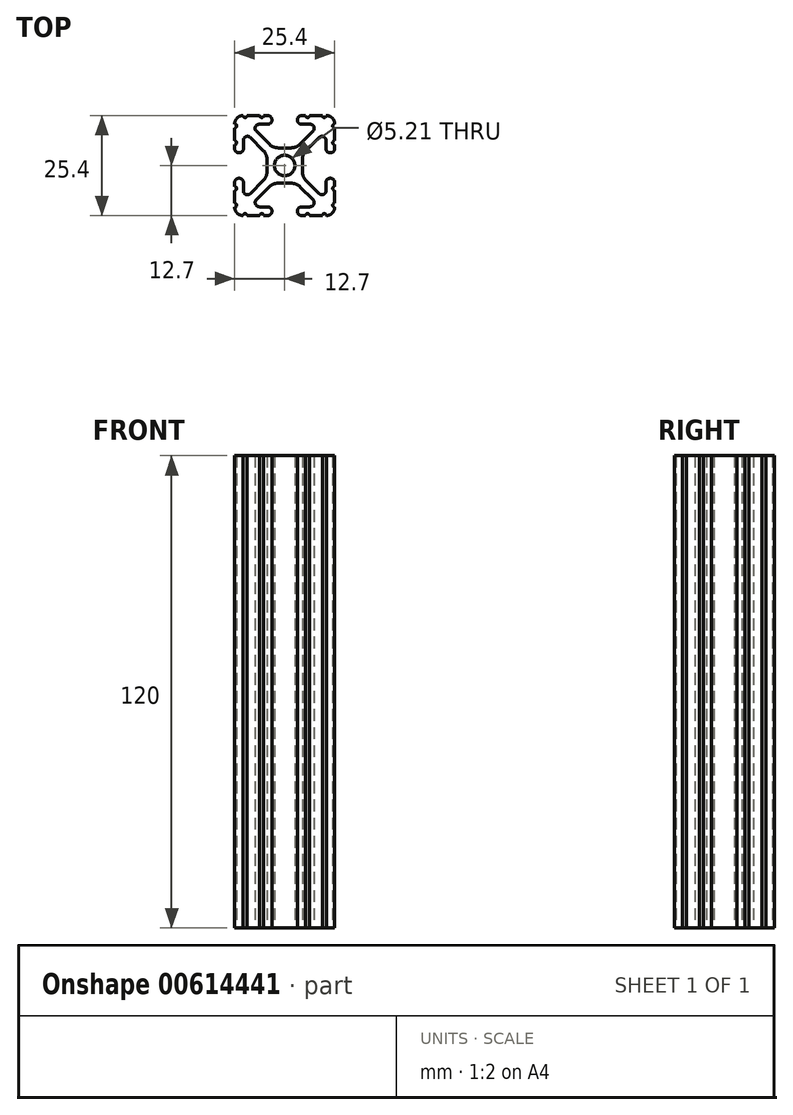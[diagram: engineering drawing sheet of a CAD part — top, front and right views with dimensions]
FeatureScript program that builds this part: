
annotation { "Feature Type Name" : "Feature", "Feature Type Description" : "" }
export const myFeature = defineFeature(function(context is Context, id is Id, definition is map)
    precondition{}
    {
        {
            var Q0;
            Q0=qCreatedBy(makeId("Top.planeOp"),FACE);
            var sketch = newSketch(context, id + "F0", { "sketchPlane" : qUnion([Q0])});
            skCircle(sketch, "E0", {"center": v(0, 0) * mm, "radius": 2.6 * mm});
            skArc(sketch, "E1", {"start": v(-1.7, -4.5) * mm, "mid": v(-2.92, -4.74) * mm, "end": v(-3.95, -5.42) * mm});
            skLineSegment(sketch, "E2", {"start": v(-1.7, -4.5) * mm, "end": v(1.7, -4.5) * mm});
            skArc(sketch, "E3", {"start": v(3.95, -5.42) * mm, "mid": v(2.92, -4.74) * mm, "end": v(1.7, -4.5) * mm});
            skLineSegment(sketch, "E4", {"start": v(3.95, -5.42) * mm, "end": v(7.18, -8.65) * mm});
            skArc(sketch, "E5", {"start": v(6.42, -10.5) * mm, "mid": v(7.41, -9.82) * mm, "end": v(7.18, -8.65) * mm});
            skLineSegment(sketch, "E6", {"start": v(6.42, -10.5) * mm, "end": v(4.29, -10.5) * mm});
            skArc(sketch, "E7", {"start": v(4.29, -10.5) * mm, "mid": v(3.55, -10.8) * mm, "end": v(3.24, -11.54) * mm});
            skLineSegment(sketch, "E8", {"start": v(3.24, -11.54) * mm, "end": v(3.24, -11.65) * mm});
            skArc(sketch, "E9", {"start": v(3.24, -11.65) * mm, "mid": v(3.55, -12.4) * mm, "end": v(4.29, -12.7) * mm});
            skLineSegment(sketch, "E10", {"start": v(4.29, -12.7) * mm, "end": v(5.32, -12.7) * mm});
            skArc(sketch, "E11", {"start": v(6.33, -12.7) * mm, "mid": v(5.83, -12.2) * mm, "end": v(5.32, -12.7) * mm});
            skLineSegment(sketch, "E12", {"start": v(6.33, -12.7) * mm, "end": v(9.55, -12.7) * mm});
            skArc(sketch, "E13", {"start": v(10.57, -12.7) * mm, "mid": v(10.06, -12.2) * mm, "end": v(9.55, -12.7) * mm});
            skArc(sketch, "E14", {"start": v(10.57, -12.7) * mm, "mid": v(12.08, -12.08) * mm, "end": v(12.7, -10.57) * mm});
            skArc(sketch, "E15", {"start": v(12.7, -9.55) * mm, "mid": v(12.2, -10.06) * mm, "end": v(12.7, -10.57) * mm});
            skLineSegment(sketch, "E16", {"start": v(12.7, -9.55) * mm, "end": v(12.7, -6.33) * mm});
            skArc(sketch, "E17", {"start": v(12.7, -5.32) * mm, "mid": v(12.2, -5.83) * mm, "end": v(12.7, -6.33) * mm});
            skLineSegment(sketch, "E18", {"start": v(12.7, -5.32) * mm, "end": v(12.7, -4.29) * mm});
            skArc(sketch, "E19", {"start": v(12.7, -4.29) * mm, "mid": v(12.4, -3.55) * mm, "end": v(11.65, -3.24) * mm});
            skLineSegment(sketch, "E20", {"start": v(11.65, -3.24) * mm, "end": v(11.54, -3.24) * mm});
            skArc(sketch, "E21", {"start": v(11.54, -3.24) * mm, "mid": v(10.8, -3.55) * mm, "end": v(10.5, -4.29) * mm});
            skLineSegment(sketch, "E22", {"start": v(10.5, -4.29) * mm, "end": v(10.5, -6.4) * mm});
            skArc(sketch, "E23", {"start": v(8.74, -7.13) * mm, "mid": v(9.86, -7.35) * mm, "end": v(10.5, -6.4) * mm});
            skLineSegment(sketch, "E24", {"start": v(8.74, -7.13) * mm, "end": v(5.44, -3.84) * mm});
            skArc(sketch, "E25", {"start": v(4.5, -1.6) * mm, "mid": v(4.75, -2.8) * mm, "end": v(5.44, -3.84) * mm});
            skLineSegment(sketch, "E26", {"start": v(4.5, -1.6) * mm, "end": v(4.5, 1.6) * mm});
            skArc(sketch, "E27", {"start": v(5.44, 3.84) * mm, "mid": v(4.75, 2.8) * mm, "end": v(4.5, 1.6) * mm});
            skLineSegment(sketch, "E28", {"start": v(5.44, 3.84) * mm, "end": v(8.74, 7.13) * mm});
            skArc(sketch, "E29", {"start": v(10.5, 6.4) * mm, "mid": v(9.86, 7.35) * mm, "end": v(8.74, 7.13) * mm});
            skLineSegment(sketch, "E30", {"start": v(10.5, 6.4) * mm, "end": v(10.5, 4.29) * mm});
            skArc(sketch, "E31", {"start": v(10.5, 4.29) * mm, "mid": v(10.8, 3.55) * mm, "end": v(11.54, 3.24) * mm});
            skLineSegment(sketch, "E32", {"start": v(11.54, 3.24) * mm, "end": v(11.65, 3.24) * mm});
            skArc(sketch, "E33", {"start": v(11.65, 3.24) * mm, "mid": v(12.4, 3.55) * mm, "end": v(12.7, 4.29) * mm});
            skLineSegment(sketch, "E34", {"start": v(12.7, 4.29) * mm, "end": v(12.7, 5.32) * mm});
            skArc(sketch, "E35", {"start": v(12.7, 6.33) * mm, "mid": v(12.2, 5.83) * mm, "end": v(12.7, 5.32) * mm});
            skLineSegment(sketch, "E36", {"start": v(12.7, 6.33) * mm, "end": v(12.7, 9.55) * mm});
            skArc(sketch, "E37", {"start": v(12.7, 10.57) * mm, "mid": v(12.2, 10.06) * mm, "end": v(12.7, 9.55) * mm});
            skArc(sketch, "E38", {"start": v(12.7, 10.57) * mm, "mid": v(12.08, 12.08) * mm, "end": v(10.57, 12.7) * mm});
            skArc(sketch, "E39", {"start": v(9.55, 12.7) * mm, "mid": v(10.06, 12.2) * mm, "end": v(10.57, 12.7) * mm});
            skLineSegment(sketch, "E40", {"start": v(9.55, 12.7) * mm, "end": v(6.33, 12.7) * mm});
            skArc(sketch, "E41", {"start": v(5.32, 12.7) * mm, "mid": v(5.83, 12.2) * mm, "end": v(6.33, 12.7) * mm});
            skLineSegment(sketch, "E42", {"start": v(5.32, 12.7) * mm, "end": v(4.29, 12.7) * mm});
            skArc(sketch, "E43", {"start": v(4.29, 12.7) * mm, "mid": v(3.55, 12.4) * mm, "end": v(3.24, 11.65) * mm});
            skLineSegment(sketch, "E44", {"start": v(3.24, 11.65) * mm, "end": v(3.24, 11.54) * mm});
            skArc(sketch, "E45", {"start": v(3.24, 11.54) * mm, "mid": v(3.55, 10.8) * mm, "end": v(4.29, 10.5) * mm});
            skLineSegment(sketch, "E46", {"start": v(4.29, 10.5) * mm, "end": v(6.48, 10.5) * mm});
            skArc(sketch, "E47", {"start": v(7.2, 8.72) * mm, "mid": v(7.43, 9.85) * mm, "end": v(6.48, 10.5) * mm});
            skLineSegment(sketch, "E48", {"start": v(7.2, 8.72) * mm, "end": v(3.9, 5.42) * mm});
            skArc(sketch, "E49", {"start": v(1.66, 4.5) * mm, "mid": v(2.87, 4.74) * mm, "end": v(3.9, 5.42) * mm});
            skLineSegment(sketch, "E50", {"start": v(1.66, 4.5) * mm, "end": v(-1.66, 4.5) * mm});
            skArc(sketch, "E51", {"start": v(-3.9, 5.42) * mm, "mid": v(-2.87, 4.74) * mm, "end": v(-1.66, 4.5) * mm});
            skLineSegment(sketch, "E52", {"start": v(-3.9, 5.42) * mm, "end": v(-7.2, 8.72) * mm});
            skArc(sketch, "E53", {"start": v(-6.48, 10.5) * mm, "mid": v(-7.43, 9.85) * mm, "end": v(-7.2, 8.72) * mm});
            skLineSegment(sketch, "E54", {"start": v(-6.48, 10.5) * mm, "end": v(-4.29, 10.5) * mm});
            skArc(sketch, "E55", {"start": v(-4.29, 10.5) * mm, "mid": v(-3.55, 10.8) * mm, "end": v(-3.24, 11.54) * mm});
            skLineSegment(sketch, "E56", {"start": v(-3.24, 11.54) * mm, "end": v(-3.24, 11.65) * mm});
            skArc(sketch, "E57", {"start": v(-3.24, 11.65) * mm, "mid": v(-3.55, 12.4) * mm, "end": v(-4.29, 12.7) * mm});
            skLineSegment(sketch, "E58", {"start": v(-4.29, 12.7) * mm, "end": v(-5.32, 12.7) * mm});
            skArc(sketch, "E59", {"start": v(-6.33, 12.7) * mm, "mid": v(-5.83, 12.2) * mm, "end": v(-5.32, 12.7) * mm});
            skLineSegment(sketch, "E60", {"start": v(-6.33, 12.7) * mm, "end": v(-9.55, 12.7) * mm});
            skArc(sketch, "E61", {"start": v(-10.57, 12.7) * mm, "mid": v(-10.06, 12.2) * mm, "end": v(-9.55, 12.7) * mm});
            skArc(sketch, "E62", {"start": v(-10.57, 12.7) * mm, "mid": v(-12.08, 12.08) * mm, "end": v(-12.7, 10.57) * mm});
            skArc(sketch, "E63", {"start": v(-12.7, 9.55) * mm, "mid": v(-12.2, 10.06) * mm, "end": v(-12.7, 10.57) * mm});
            skLineSegment(sketch, "E64", {"start": v(-12.7, 9.55) * mm, "end": v(-12.7, 6.33) * mm});
            skArc(sketch, "E65", {"start": v(-12.7, 5.32) * mm, "mid": v(-12.2, 5.83) * mm, "end": v(-12.7, 6.33) * mm});
            skLineSegment(sketch, "E66", {"start": v(-12.7, 5.32) * mm, "end": v(-12.7, 4.29) * mm});
            skArc(sketch, "E67", {"start": v(-12.7, 4.29) * mm, "mid": v(-12.4, 3.55) * mm, "end": v(-11.65, 3.24) * mm});
            skLineSegment(sketch, "E68", {"start": v(-11.65, 3.24) * mm, "end": v(-11.54, 3.24) * mm});
            skArc(sketch, "E69", {"start": v(-11.54, 3.24) * mm, "mid": v(-10.8, 3.55) * mm, "end": v(-10.5, 4.29) * mm});
            skLineSegment(sketch, "E70", {"start": v(-10.5, 4.29) * mm, "end": v(-10.5, 6.4) * mm});
            skArc(sketch, "E71", {"start": v(-8.74, 7.13) * mm, "mid": v(-9.86, 7.35) * mm, "end": v(-10.5, 6.4) * mm});
            skLineSegment(sketch, "E72", {"start": v(-8.74, 7.13) * mm, "end": v(-5.44, 3.84) * mm});
            skArc(sketch, "E73", {"start": v(-4.5, 1.6) * mm, "mid": v(-4.75, 2.8) * mm, "end": v(-5.44, 3.84) * mm});
            skLineSegment(sketch, "E74", {"start": v(-4.5, 1.6) * mm, "end": v(-4.5, -1.6) * mm});
            skArc(sketch, "E75", {"start": v(-5.44, -3.84) * mm, "mid": v(-4.75, -2.8) * mm, "end": v(-4.5, -1.6) * mm});
            skLineSegment(sketch, "E76", {"start": v(-5.44, -3.84) * mm, "end": v(-8.74, -7.13) * mm});
            skArc(sketch, "E77", {"start": v(-10.5, -6.4) * mm, "mid": v(-9.86, -7.35) * mm, "end": v(-8.74, -7.13) * mm});
            skLineSegment(sketch, "E78", {"start": v(-10.5, -6.4) * mm, "end": v(-10.5, -4.29) * mm});
            skArc(sketch, "E79", {"start": v(-10.5, -4.29) * mm, "mid": v(-10.8, -3.55) * mm, "end": v(-11.54, -3.24) * mm});
            skLineSegment(sketch, "E80", {"start": v(-11.54, -3.24) * mm, "end": v(-11.65, -3.24) * mm});
            skArc(sketch, "E81", {"start": v(-11.65, -3.24) * mm, "mid": v(-12.4, -3.55) * mm, "end": v(-12.7, -4.29) * mm});
            skLineSegment(sketch, "E82", {"start": v(-12.7, -4.29) * mm, "end": v(-12.7, -5.32) * mm});
            skArc(sketch, "E83", {"start": v(-12.7, -6.33) * mm, "mid": v(-12.2, -5.83) * mm, "end": v(-12.7, -5.32) * mm});
            skLineSegment(sketch, "E84", {"start": v(-12.7, -6.33) * mm, "end": v(-12.7, -9.55) * mm});
            skArc(sketch, "E85", {"start": v(-12.7, -10.57) * mm, "mid": v(-12.2, -10.06) * mm, "end": v(-12.7, -9.55) * mm});
            skArc(sketch, "E86", {"start": v(-12.7, -10.57) * mm, "mid": v(-12.08, -12.08) * mm, "end": v(-10.57, -12.7) * mm});
            skArc(sketch, "E87", {"start": v(-9.55, -12.7) * mm, "mid": v(-10.06, -12.2) * mm, "end": v(-10.57, -12.7) * mm});
            skLineSegment(sketch, "E88", {"start": v(-9.55, -12.7) * mm, "end": v(-6.33, -12.7) * mm});
            skArc(sketch, "E89", {"start": v(-5.32, -12.7) * mm, "mid": v(-5.83, -12.2) * mm, "end": v(-6.33, -12.7) * mm});
            skLineSegment(sketch, "E90", {"start": v(-5.32, -12.7) * mm, "end": v(-4.29, -12.7) * mm});
            skArc(sketch, "E91", {"start": v(-4.29, -12.7) * mm, "mid": v(-3.55, -12.4) * mm, "end": v(-3.24, -11.65) * mm});
            skLineSegment(sketch, "E92", {"start": v(-3.24, -11.65) * mm, "end": v(-3.24, -11.54) * mm});
            skArc(sketch, "E93", {"start": v(-3.24, -11.54) * mm, "mid": v(-3.55, -10.8) * mm, "end": v(-4.29, -10.5) * mm});
            skLineSegment(sketch, "E94", {"start": v(-4.29, -10.5) * mm, "end": v(-6.42, -10.5) * mm});
            skArc(sketch, "E95", {"start": v(-7.18, -8.65) * mm, "mid": v(-7.41, -9.82) * mm, "end": v(-6.42, -10.5) * mm});
            skLineSegment(sketch, "E96", {"start": v(-7.18, -8.65) * mm, "end": v(-3.95, -5.42) * mm});
            skSolve(sketch);
        }
        {
            var Q0;
            Q0 = qSketchRegion(id + "F0", true);
            extrude(context, id + "F1", {"entities" : qUnion([Q0]), "depth" : 120 * mm, "offsetDistance" : 25 * mm});
        }
    });
